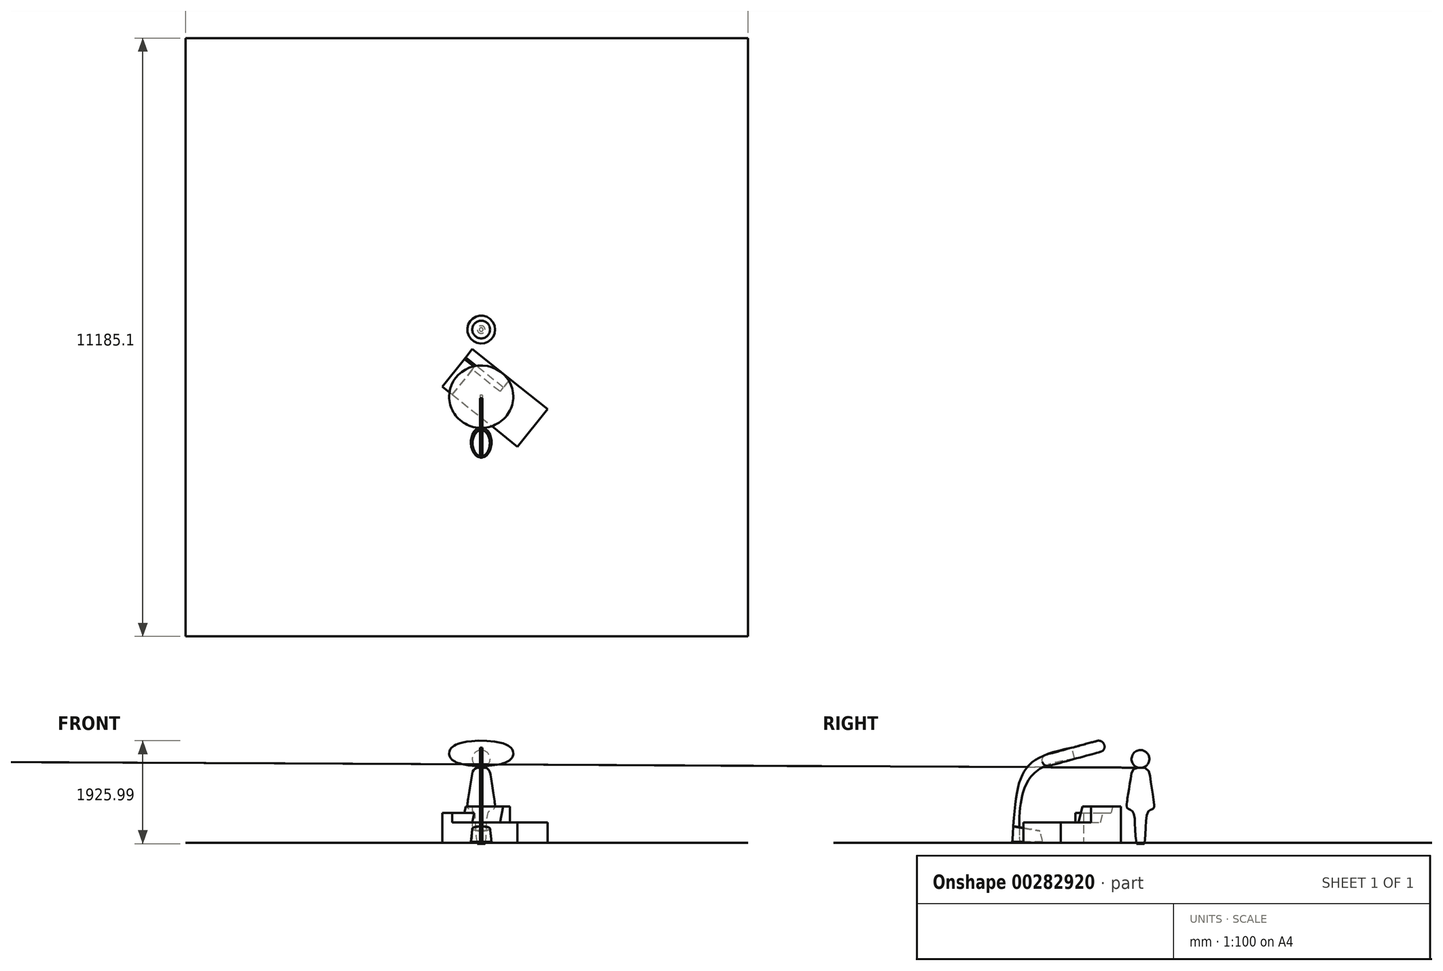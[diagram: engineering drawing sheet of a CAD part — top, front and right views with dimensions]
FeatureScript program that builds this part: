
annotation { "Feature Type Name" : "Feature", "Feature Type Description" : "" }
export const myFeature = defineFeature(function(context is Context, id is Id, definition is map)
    precondition{}
    {
        {
            var Q0;
            Q0=qCreatedBy(makeId("Right.planeOp"),FACE);
            var sketch = newSketch(context, id + "F0", { "sketchPlane" : qUnion([Q0])});
            skFitSpline(sketch, "E0", {"points": [v(0, 0) * mm, v(1246.4, 1800) * mm], "startDerivative": vector(236.54, 4063.73) * mm, "endDerivative": vector(3451.06, 599.34) * mm});
            skFitSpline(sketch, "E1", {"points": [v(1167.53, 1567.75) * mm, v(456.36, 1341.56) * mm, v(136.65, 0) * mm], "startDerivative": vector(-2339.04, -348.16) * mm, "endDerivative": vector(233.2, -4364.36) * mm});
            skLineSegment(sketch, "E2", {"start": v(136.65, 0) * mm, "end": v(0, 0) * mm});
            skLineSegment(sketch, "E3", {"start": v(1167.53, 1567.75) * mm, "end": v(1111.39, 1775.29) * mm});
            skSolve(sketch);
        }
        {
            var Q0;
            Q0 = qSketchRegion(id + "F0", true);
            extrude(context, id + "F1", {"entities" : qUnion([Q0]), "depth" : 25 * mm, "hasSecondDirection" : true, "secondDirectionOppositeDirection" : true, "secondDirectionDepth" : 25 * mm});
        }
        {
            var Q0;
            Q0=qCreatedBy(makeId("Right.planeOp"),FACE);
            var sketch = newSketch(context, id + "F2", { "sketchPlane" : qUnion([Q0])});
            skLineSegment(sketch, "E4.0", {"start": v(1167.53, 1567.75) * mm, "end": v(1111.39, 1775.29) * mm});
            skLineSegment(sketch, "E5", {"start": v(1139.46, 1671.52) * mm, "end": v(560.28, 1514.83) * mm});
            skEllipse(sketch, "E6", {"center": v(1139.46, 1671.52) * mm, "majorRadius": 107.5 * mm, "minorRadius": 600 * mm, "majorAxis": v(-0.26, 0.97)});
            skSolve(sketch);
        }
        {
            var Q0;
            Q0=qCreatedBy(makeId("Right.planeOp"),FACE);
            var sketch = newSketch(context, id + "F3", { "sketchPlane" : qUnion([Q0])});
            skEllipticalArc(sketch, "E7.0", {"construction": true});
            skLineSegment(sketch, "E8", {"start": v(1111.39, 1775.29) * mm, "end": v(1167.53, 1567.75) * mm});
            skLineSegment(sketch, "E9", {"start": v(1139.46, 1671.52) * mm, "end": v(560.28, 1525.6) * mm, "construction": true});
            skPoint(sketch, "E9.endSnap0", {"position": v(560.28, 1514.83) * mm});
            skLineSegment(sketch, "E10", {"start": v(1111.39, 1775.29) * mm, "end": v(532.2, 1618.6) * mm});
            skLineSegment(sketch, "E11", {"start": v(532.2, 1618.6) * mm, "end": v(588.36, 1411.06) * mm});
            skLineSegment(sketch, "E12", {"start": v(1167.53, 1567.75) * mm, "end": v(588.36, 1411.06) * mm});
            const initialGuessF3  = {"E7.0": [1.141330909394251, 1.6646051492458063, -0.9652978506633573, -0.26115141107162915, 0.6, 0.1075, 4.71238898038469, 1.5707963267948966]};
            skSetInitialGuess(sketch, initialGuessF3);
            skSolve(sketch);
        }
        {
            var Q0;
            Q0 = qSketchRegion(id + "F3", true);
            var Q1;
            Q1=sQuery(id+"F3.wireOp",EDGE,"E8");
            revolve(context, id + "F4", {"entities" : qUnion([Q0]), "axis" : qUnion([Q1]), "revolveType" : RevolveType.FULL});
        }
        {
            var Q0;
            Q0=qCreatedBy(makeId("Top.planeOp"),FACE);
            var sketch = newSketch(context, id + "F5", { "sketchPlane" : qUnion([Q0])});
            skEllipse(sketch, "E13", {"center": v(0, 285) * mm, "majorRadius": 285 * mm, "minorRadius": 194.8 * mm, "majorAxis": v(0, -1)});
            skLineSegment(sketch, "E14", {"start": v(0, 285) * mm, "end": v(0, 570) * mm});
            skSolve(sketch);
        }
        {
            var Q0;
            Q0=qCreatedBy(makeId("Right.planeOp"),FACE);
            var sketch = newSketch(context, id + "F6", { "sketchPlane" : qUnion([Q0])});
            skLineSegment(sketch, "E15", {"start": v(23.8, 308.2) * mm, "end": v(534.7, 218.82) * mm});
            skSolve(sketch);
        }
        {
            var Q0;
            Q0=sQuery(id+"F6.wireOp",EDGE,"E15");
            cPlane(context, id + "F7", {"entities" : qUnion([Q0]), "cplaneType" : CPlaneType.LINE_ANGLE, "offset" : 25 * mm, "angle" : 0 * degree, "width" : 150 * mm, "height" : 150 * mm});
        }
        {
            var Q0;
            Q0=qCreatedBy(id+"F7.planeOp",FACE);
            var sketch = newSketch(context, id + "F8", { "sketchPlane" : qUnion([Q0])});
            skEllipse(sketch, "E16", {"center": v(0, 220.33) * mm, "majorRadius": 250 * mm, "minorRadius": 165 * mm, "majorAxis": v(0, -1)});
            skLineSegment(sketch, "E17", {"start": v(0, 220.33) * mm, "end": v(0, 470.33) * mm});
            skSolve(sketch);
        }
        {
            var Q1;
            Q1=makeQuery(id+"F5.imprint","IMPRINT",FACE,{"disambiguationData":[TD([[makeQuery(id+"F5.imprint","IMPRINT",EDGE,{"derivedFrom":sQuery(id+"F5.wireOp",EDGE,"E13")}),1.0]])]});
            var Q2;
            Q2=makeQuery(id+"F8.imprint","IMPRINT",FACE,{"disambiguationData":[TD([[makeQuery(id+"F8.imprint","IMPRINT",EDGE,{"derivedFrom":sQuery(id+"F8.wireOp",EDGE,"E16")}),1.0]])]});
            loft(context, id + "F9", {"sheetProfilesArray" : [{ "sheetProfileEntities" : qUnion([Q1]) }, { "sheetProfileEntities" : qUnion([Q2]) }]});
        }
        {
            var Q0;
            Q0=makeQuery(id+"F9.opLoft","MID_CAP_EDGE",EDGE,{"disambiguationData":[OSD([sQuery(id+"F5.wireOp",EDGE,"E13"),sQuery(id+"F8.wireOp",EDGE,"E16")])],"capPos":1.0});
            fillet(context, id + "F10", {"entities" : qUnion([Q0]), "radius" : 5 * mm, "tangentPropagation" : true, "allowEdgeOverflow" : false});
        }
        {
            var Q0;
            Q0=makeQuery(id+"F9.opLoft","CAP_FACE",FACE,{"disambiguationData":[OSD([makeQuery(id+"F5.imprint","IMPRINT",FACE,{"disambiguationData":[TD([[makeQuery(id+"F5.imprint","IMPRINT",EDGE,{"derivedFrom":sQuery(id+"F5.wireOp",EDGE,"E13")}),1.0]])]})])],"isStart":true});
            chamfer(context, id + "F11", {"entities" : qUnion([Q0]), "width" : 15 * mm, "tangentPropagation" : true});
        }
        {
            var Q0;
            Q0=qCreatedBy(makeId("Right.planeOp"),FACE);
            var sketch = newSketch(context, id + "F12", { "sketchPlane" : qUnion([Q0])});
            skLineSegment(sketch, "E18", {"start": v(-1237.65, -18.92) * mm, "end": v(5514.82, -18.92) * mm, "construction": true});
            skLineSegment(sketch, "E19", {"start": v(2395.16, 1853.97) * mm, "end": v(2395.16, -18.92) * mm, "construction": true});
            skPoint(sketch, "E20.3.internal.snap0", {"position": v(2138.59, -18.92) * mm});
            skFitSpline(sketch, "E20", {"points": [v(2323.36, -18.92) * mm, v(2253.59, 578.32) * mm, v(2152.07, 639.97) * mm, v(2138.59, 720.85) * mm, v(2212.68, 1213.92) * mm, v(2395.16, 1398.54) * mm], "startDerivative": vector(-517.63, 2307.26) * mm, "endDerivative": vector(2361.92, -362.1) * mm});
            skArc(sketch, "E21", {"start": v(2395.16, 1731.08) * mm, "mid": v(2228.89, 1564.8) * mm, "end": v(2395.16, 1398.54) * mm});
            skLineSegment(sketch, "E22", {"start": v(2395.16, 1731.08) * mm, "end": v(2395.16, -18.92) * mm});
            skLineSegment(sketch, "E23", {"start": v(2323.36, -18.92) * mm, "end": v(2395.16, -18.92) * mm});
            skSolve(sketch);
        }
        {
            var Q0;
            Q0 = qSketchRegion(id + "F12", true);
            var Q1;
            Q1=sQuery(id+"F12.wireOp",EDGE,"E19");
            revolve(context, id + "F13", {"entities" : qUnion([Q0]), "axis" : qUnion([Q1]), "revolveType" : RevolveType.FULL});
        }
        {
            var Q0;
            Q0=qCreatedBy(makeId("Top.planeOp"),FACE);
            var sketch = newSketch(context, id + "F14", { "sketchPlane" : qUnion([Q0])});
            skLineSegment(sketch, "E24.bottom", {"start": v(-5528.86, -3341.54) * mm, "end": v(4989.84, -3341.54) * mm});
            skLineSegment(sketch, "E24.top", {"start": v(-5528.86, 7843.55) * mm, "end": v(4989.84, 7843.55) * mm});
            skLineSegment(sketch, "E24.left", {"start": v(-5528.86, -3341.54) * mm, "end": v(-5528.86, 7843.55) * mm});
            skLineSegment(sketch, "E24.right", {"start": v(4989.84, -3341.54) * mm, "end": v(4989.84, 7843.55) * mm});
            skSolve(sketch);
        }
        {
            var Q0;
            Q0 = qSketchRegion(id + "F14", true);
            extrude(context, id + "F15", {"entities" : qUnion([Q0]), "oppositeDirection" : true, "depth" : 5 * mm});
        }
        {
            var Q0;
            Q0=qCreatedBy(makeId("Top.planeOp"),FACE);
            var sketch = newSketch(context, id + "F16", { "sketchPlane" : qUnion([Q0])});
            skLineSegment(sketch, "E25", {"start": v(679.3, 204.66) * mm, "end": v(1240.86, 907.97) * mm});
            skLineSegment(sketch, "E26", {"start": v(1240.86, 907.97) * mm, "end": v(537.54, 1469.53) * mm});
            skLineSegment(sketch, "E27", {"start": v(537.54, 1469.53) * mm, "end": v(-24.02, 766.22) * mm});
            skLineSegment(sketch, "E28", {"start": v(-24.02, 766.22) * mm, "end": v(679.3, 204.66) * mm});
            skSolve(sketch);
        }
        {
            var Q0;
            Q0=makeQuery(id+"F16.imprint","IMPRINT",FACE,{"disambiguationData":[TD([[makeQuery(id+"F16.imprint","IMPRINT",EDGE,{"derivedFrom":sQuery(id+"F16.wireOp",EDGE,"E25")}),1.0]])]});
            extrude(context, id + "F17", {"entities" : qUnion([Q0]), "depth" : 380 * mm});
        }
        {
            var Q0;
            Q0=qCreatedBy(makeId("Top.planeOp"),FACE);
            var sketch = newSketch(context, id + "F18", { "sketchPlane" : qUnion([Q0])});
            skLineSegment(sketch, "E29", {"start": v(537.54, 1469.53) * mm, "end": v(-24.02, 766.22) * mm});
            skLineSegment(sketch, "E30", {"start": v(-24.02, 766.22) * mm, "end": v(-727.33, 1327.78) * mm});
            skLineSegment(sketch, "E31", {"start": v(-727.33, 1327.78) * mm, "end": v(-165.77, 2031.1) * mm});
            skLineSegment(sketch, "E32", {"start": v(-165.77, 2031.1) * mm, "end": v(537.54, 1469.53) * mm});
            skSolve(sketch);
        }
        {
            var Q0;
            Q0 = qSketchRegion(id + "F18", true);
            extrude(context, id + "F19", {"entities" : qUnion([Q0]), "depth" : 380 * mm});
        }
        {
            var Q0;
            Q0=makeQuery(id+"F19.opExtrude","SWEPT_FACE",FACE,{"disambiguationData":[OSD([sQuery(id+"F18.wireOp",EDGE,"E31")])]});
            var sketch = newSketch(context, id + "F20", { "sketchPlane" : qUnion([Q0])});
            skLineSegment(sketch, "E33", {"start": v(-1483.78, 0) * mm, "end": v(-1483.78, 680) * mm});
            skLineSegment(sketch, "E34", {"start": v(-1483.78, 680) * mm, "end": v(-1283.78, 680) * mm});
            skLineSegment(sketch, "E35", {"start": v(-1283.78, 680) * mm, "end": v(-1183.78, 380) * mm});
            skLineSegment(sketch, "E36", {"start": v(-1483.78, 0) * mm, "end": v(-1183.78, 380) * mm});
            skSolve(sketch);
        }
        {
            var Q0;
            Q0 = qSketchRegion(id + "F20", true);
            extrude(context, id + "F21", {"entities" : qUnion([Q0]), "operationType" : NewBodyOperationType.ADD, "oppositeDirection" : true, "depth" : 900 * mm});
        }
        {
            var Q0;
            Q0=makeQuery(id+"F21.boolean.opBoolean","MERGE",FACE,{"derivedFrom":[makeQuery(id+"F19.opExtrude","SWEPT_FACE",FACE,{"disambiguationData":[OSD([sQuery(id+"F18.wireOp",EDGE,"E31")])]}),makeQuery(id+"F21.opExtrude","CAP_FACE",FACE,{"disambiguationData":[OSD([sQuery(id+"F20.wireOp",EDGE,"E33"),sQuery(id+"F20.wireOp",EDGE,"E34"),sQuery(id+"F20.wireOp",EDGE,"E35"),sQuery(id+"F20.wireOp",EDGE,"E36")])],"isStart":true})]});
            var sketch = newSketch(context, id + "F22", { "sketchPlane" : qUnion([Q0])});
            skLineSegment(sketch, "E37.bottom", {"start": v(-583.78, 0) * mm, "end": v(-1242.78, 0) * mm});
            skLineSegment(sketch, "E37.top", {"start": v(-583.78, 557) * mm, "end": v(-1242.78, 557) * mm});
            skLineSegment(sketch, "E37.left", {"start": v(-583.78, 0) * mm, "end": v(-583.78, 557) * mm});
            skLineSegment(sketch, "E37.right", {"start": v(-1242.78, 0) * mm, "end": v(-1242.78, 557) * mm});
            skSolve(sketch);
        }
        {
            var Q0;
            Q0 = qSketchRegion(id + "F22", true);
            extrude(context, id + "F23", {"entities" : qUnion([Q0]), "operationType" : NewBodyOperationType.ADD, "oppositeDirection" : true, "depth" : 240 * mm});
        }
        {
            var Q0;
            Q0=makeQuery(id+"F4.opRevolve","SWEPT_EDGE",EDGE,{"disambiguationData":[OSD([sQuery(id+"F3.wireOp",EDGE,"E11"),sQuery(id+"F3.wireOp",EDGE,"E12")])]});
            fillet(context, id + "F24", {"entities" : qUnion([Q0]), "radius" : 100 * mm, "tangentPropagation" : true, "allowEdgeOverflow" : false});
        }
        {
            var Q0;
            Q0=makeQuery(id+"F4.opRevolve","SWEPT_EDGE",EDGE,{"disambiguationData":[OSD([sQuery(id+"F3.wireOp",EDGE,"E10"),sQuery(id+"F3.wireOp",EDGE,"E11")])]});
            fillet(context, id + "F25", {"entities" : qUnion([Q0]), "radius" : 110 * mm, "tangentPropagation" : true, "allowEdgeOverflow" : false});
        }
    });
